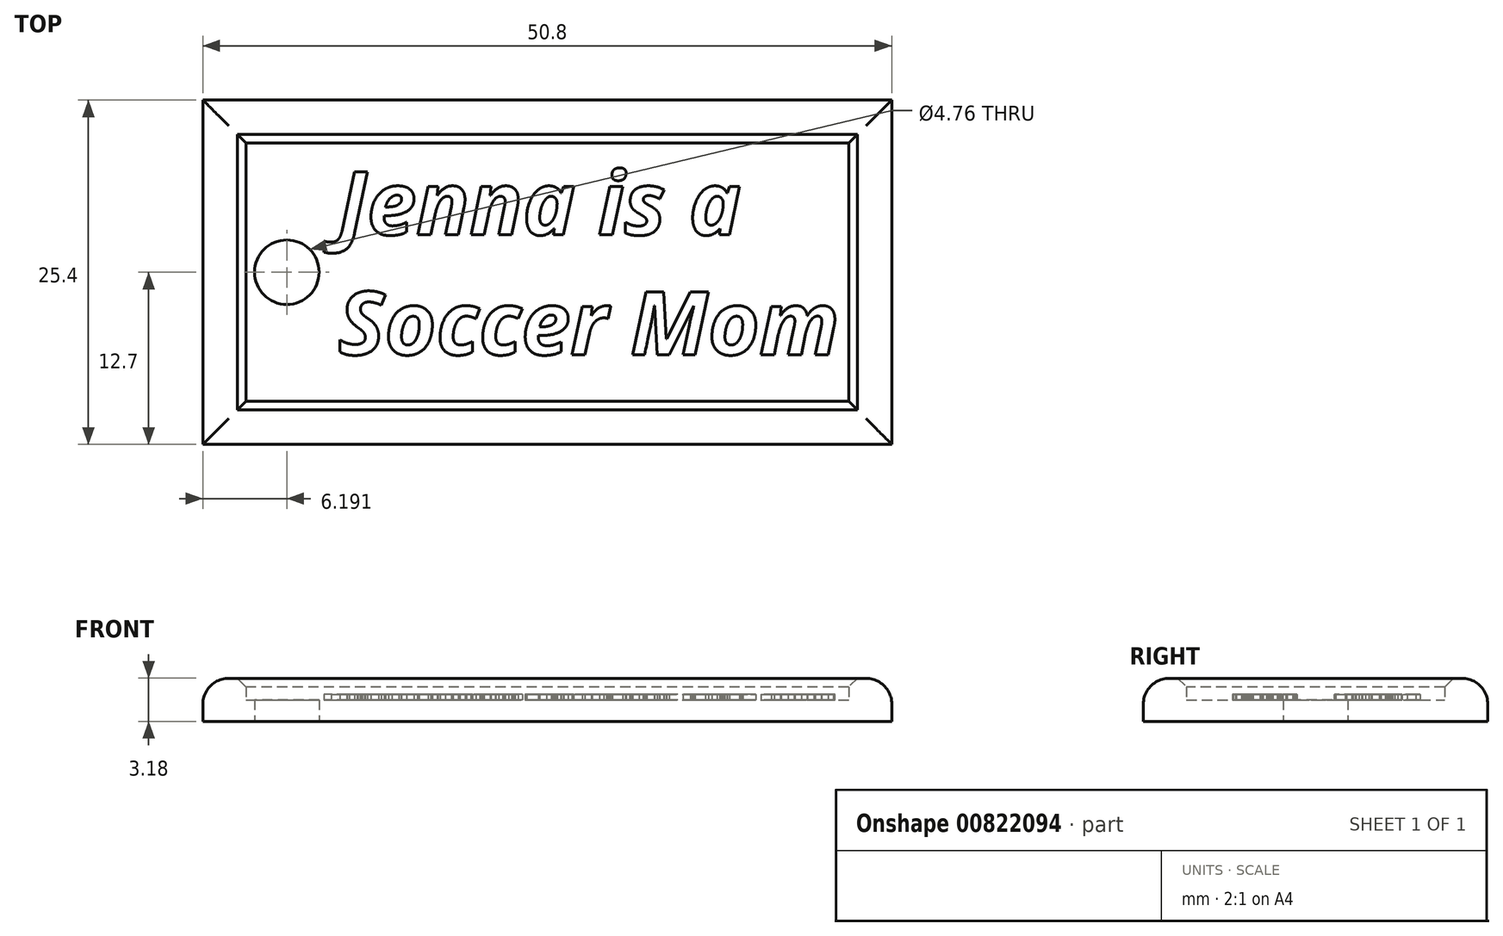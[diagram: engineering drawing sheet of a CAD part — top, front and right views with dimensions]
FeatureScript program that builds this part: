
annotation { "Feature Type Name" : "Feature", "Feature Type Description" : "" }
export const myFeature = defineFeature(function(context is Context, id is Id, definition is map)
    precondition{}
    {
        {
            var Q0;
            Q0=qCreatedBy(makeId("Top.planeOp"),FACE);
            var sketch = newSketch(context, id + "F0", { "sketchPlane" : qUnion([Q0])});
            skLineSegment(sketch, "E0.bottom", {"start": v(0, 0) * mm, "end": v(50.8, 0) * mm});
            skLineSegment(sketch, "E0.top", {"start": v(0, 25.4) * mm, "end": v(50.8, 25.4) * mm});
            skLineSegment(sketch, "E0.left", {"start": v(0, 0) * mm, "end": v(0, 25.4) * mm});
            skLineSegment(sketch, "E0.right", {"start": v(50.8, 0) * mm, "end": v(50.8, 25.4) * mm});
            skCircle(sketch, "E1", {"center": v(6.2, 12.7) * mm, "radius": 2.38 * mm});
            skPoint(sketch, "E1.centerSnap0", {"position": v(0, 12.7) * mm});
            skLineSegment(sketch, "E2.0", {"start": v(3.17, 22.23) * mm, "end": v(47.62, 22.23) * mm});
            skLineSegment(sketch, "E2.1", {"start": v(3.17, 3.18) * mm, "end": v(3.17, 22.23) * mm});
            skLineSegment(sketch, "E2.2", {"start": v(3.17, 3.18) * mm, "end": v(47.62, 3.18) * mm});
            skLineSegment(sketch, "E2.3", {"start": v(47.62, 3.18) * mm, "end": v(47.62, 22.23) * mm});
            skSolve(sketch);
        }
        {
            var Q0;
            Q0=makeQuery(id+"F0.imprint","IMPRINT",FACE,{"disambiguationData":[TD([[makeQuery(id+"F0.imprint","IMPRINT",EDGE,{"derivedFrom":sQuery(id+"F0.wireOp",EDGE,"E1")}),-1.0]])]});
            extrude(context, id + "F1", {"entities" : qUnion([Q0]), "depth" : 1.59 * mm, "offsetDistance" : 25.4 * mm});
        }
        {
            var Q0;
            Q0 = qSketchRegion(id + "F0", true);
            extrude(context, id + "F2", {"entities" : qUnion([Q0]), "operationType" : NewBodyOperationType.ADD, "depth" : 3.17 * mm, "offsetDistance" : 25.4 * mm});
        }
        {
            var Q0;
            Q0=makeQuery(id+"F2.opExtrude","CAP_EDGE",EDGE,{"disambiguationData":[OSD([sQuery(id+"F0.wireOp",EDGE,"E0.bottom")])],"isStart":false});
            var Q1;
            Q1=makeQuery(id+"F2.opExtrude","CAP_EDGE",EDGE,{"disambiguationData":[OSD([sQuery(id+"F0.wireOp",EDGE,"E0.right")])],"isStart":false});
            var Q2;
            Q2=makeQuery(id+"F2.opExtrude","CAP_EDGE",EDGE,{"disambiguationData":[OSD([sQuery(id+"F0.wireOp",EDGE,"E0.top")])],"isStart":false});
            var Q3;
            Q3=makeQuery(id+"F2.opExtrude","CAP_EDGE",EDGE,{"disambiguationData":[OSD([sQuery(id+"F0.wireOp",EDGE,"E0.left")])],"isStart":false});
            fillet(context, id + "F3", {"entities" : qUnion([Q0, Q1, Q2, Q3]), "radius" : 1.9 * mm, "tangentPropagation" : true, "allowEdgeOverflow" : false});
        }
        {
            var Q0;
            Q0=makeQuery(id+"F2.opExtrude","CAP_EDGE",EDGE,{"disambiguationData":[OSD([sQuery(id+"F0.wireOp",EDGE,"E2.0")])],"isStart":false});
            var Q1;
            Q1=makeQuery(id+"F2.opExtrude","CAP_EDGE",EDGE,{"disambiguationData":[OSD([sQuery(id+"F0.wireOp",EDGE,"E2.1")])],"isStart":false});
            var Q2;
            Q2=makeQuery(id+"F2.opExtrude","CAP_EDGE",EDGE,{"disambiguationData":[OSD([sQuery(id+"F0.wireOp",EDGE,"E2.2")])],"isStart":false});
            var Q3;
            Q3=makeQuery(id+"F2.opExtrude","CAP_EDGE",EDGE,{"disambiguationData":[OSD([sQuery(id+"F0.wireOp",EDGE,"E2.3")])],"isStart":false});
            chamfer(context, id + "F4", {"entities" : qUnion([Q0, Q1, Q2, Q3]), "width" : 0.64 * mm, "tangentPropagation" : true});
        }
        {
            var Q0;
            Q0=makeQuery(id+"F1.opExtrude","CAP_FACE",FACE,{"disambiguationData":[OSD([sQuery(id+"F0.wireOp",EDGE,"E1"),sQuery(id+"F0.wireOp",EDGE,"E2.0"),sQuery(id+"F0.wireOp",EDGE,"E2.1"),sQuery(id+"F0.wireOp",EDGE,"E2.2"),sQuery(id+"F0.wireOp",EDGE,"E2.3")])],"isStart":false});
            var sketch = newSketch(context, id + "F5", { "sketchPlane" : qUnion([Q0])});
            skText(sketch, "E3", { "text": "Jenna is a\nSoccer Mom", "fontName": "OpenSans-BoldItalic.ttf"});
            const initialGuessF5  = {"E3": [0.00996, 0.01546, 1, 0, 0.00468]};
            skSetInitialGuess(sketch, initialGuessF5);
            skSolve(sketch);
        }
        {
            var Q0;
            Q0 = qSketchRegion(id + "F5", true);
            extrude(context, id + "F6", {"entities" : qUnion([Q0]), "operationType" : NewBodyOperationType.ADD, "depth" : 0.4 * mm, "offsetDistance" : 25.4 * mm});
        }
    });
